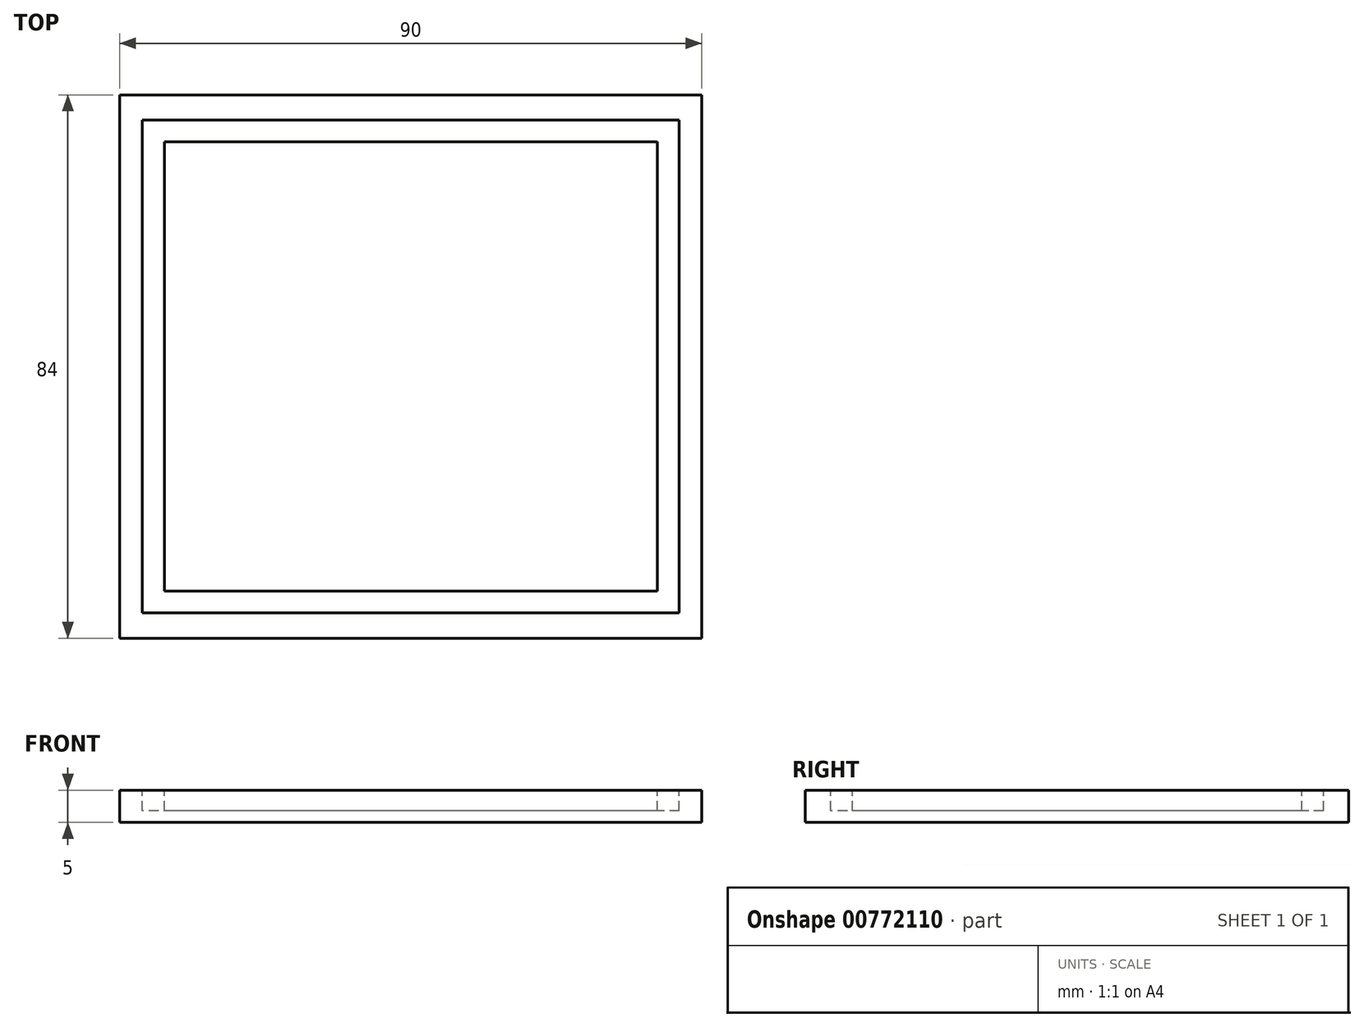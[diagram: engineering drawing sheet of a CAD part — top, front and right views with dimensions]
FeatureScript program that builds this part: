
annotation { "Feature Type Name" : "Feature", "Feature Type Description" : "" }
export const myFeature = defineFeature(function(context is Context, id is Id, definition is map)
    precondition{}
    {
        {
            var Q0;
            Q0=qCreatedBy(makeId("Top.planeOp"),FACE);
            var sketch = newSketch(context, id + "F0", { "sketchPlane" : qUnion([Q0])});
            skLineSegment(sketch, "E0.bottom", {"start": v(45, 42) * mm, "end": v(-45, 42) * mm});
            skLineSegment(sketch, "E0.top", {"start": v(45, -42) * mm, "end": v(-45, -42) * mm});
            skLineSegment(sketch, "E0.left", {"start": v(45, 42) * mm, "end": v(45, -42) * mm});
            skLineSegment(sketch, "E0.right", {"start": v(-45, 42) * mm, "end": v(-45, -42) * mm});
            skPoint(sketch, "E0.middle", {"position": v(0, 0) * mm});
            skSolve(sketch);
        }
        {
            var Q0;
            Q0=qSketchRegion(id+"F0",true);
            extrude(context, id + "F1", {"entities" : qUnion([Q0]), "depth" : 5 * mm, "offsetDistance" : 25 * mm});
        }
        {
            var Q0;
            Q0=makeQuery(id+"F1.opExtrude","CAP_FACE",FACE,{"disambiguationData":[OSD([sQuery(id+"F0.wireOp",EDGE,"E0.bottom"),sQuery(id+"F0.wireOp",EDGE,"E0.top"),sQuery(id+"F0.wireOp",EDGE,"E0.left"),sQuery(id+"F0.wireOp",EDGE,"E0.right")])],"isStart":false});
            var sketch = newSketch(context, id + "F2", { "sketchPlane" : qUnion([Q0])});
            skLineSegment(sketch, "E1.bottom", {"start": v(41.5, 38.1) * mm, "end": v(-41.5, 38.1) * mm});
            skLineSegment(sketch, "E1.top", {"start": v(41.5, -38.1) * mm, "end": v(-41.5, -38.1) * mm});
            skLineSegment(sketch, "E1.left", {"start": v(41.5, 38.1) * mm, "end": v(41.5, -38.1) * mm});
            skLineSegment(sketch, "E1.right", {"start": v(-41.5, 38.1) * mm, "end": v(-41.5, -38.1) * mm});
            skPoint(sketch, "E1.middle", {"position": v(0, 0) * mm});
            skLineSegment(sketch, "E2.bottom", {"start": v(38.1, 34.75) * mm, "end": v(-38.1, 34.75) * mm});
            skLineSegment(sketch, "E2.top", {"start": v(38.1, -34.75) * mm, "end": v(-38.1, -34.75) * mm});
            skLineSegment(sketch, "E2.left", {"start": v(38.1, 34.75) * mm, "end": v(38.1, -34.75) * mm});
            skLineSegment(sketch, "E2.right", {"start": v(-38.1, 34.75) * mm, "end": v(-38.1, -34.75) * mm});
            skSolve(sketch);
        }
        {
            var Q0;
            Q0=qSketchRegion(id+"F2",true);
            extrude(context, id + "F3", {"entities" : qUnion([Q0]), "operationType" : NewBodyOperationType.REMOVE, "oppositeDirection" : true, "depth" : 3.2 * mm, "offsetDistance" : 25 * mm});
        }
    });
